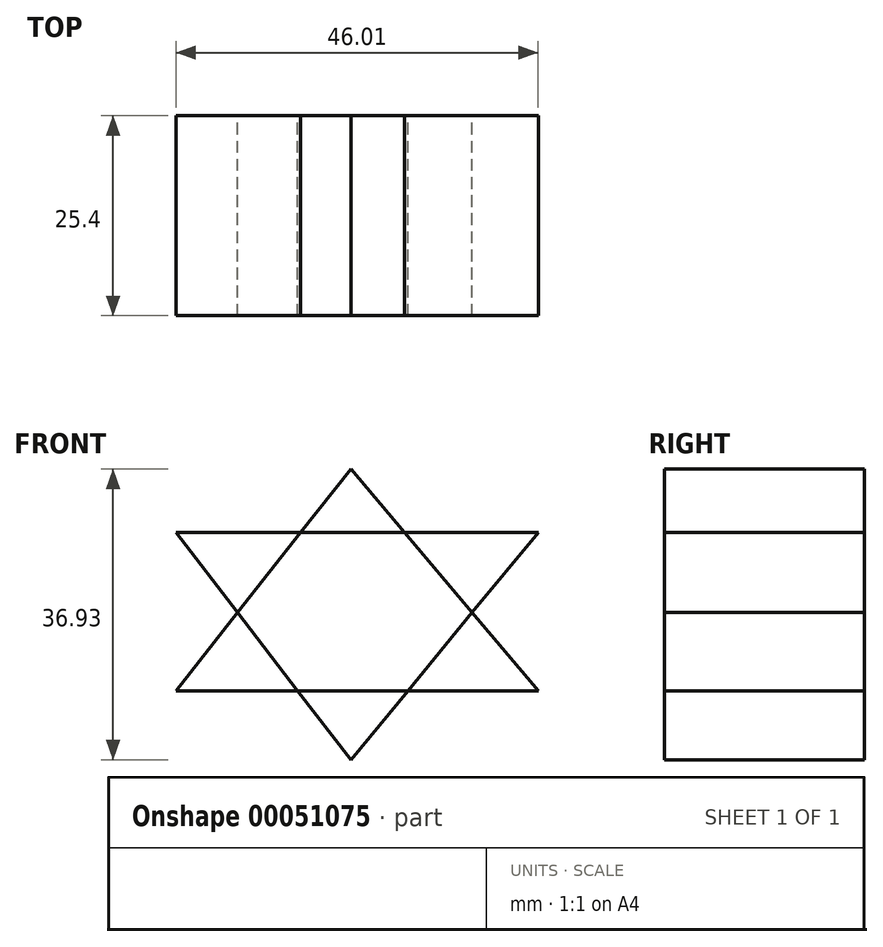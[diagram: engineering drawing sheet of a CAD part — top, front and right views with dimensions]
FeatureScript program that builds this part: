
annotation { "Feature Type Name" : "Feature", "Feature Type Description" : "" }
export const myFeature = defineFeature(function(context is Context, id is Id, definition is map)
    precondition{}
    {
        {
            var Q0;
            Q0=qCreatedBy(makeId("Front.planeOp"),FACE);
            var sketch = newSketch(context, id + "F0", { "sketchPlane" : qUnion([Q0])});
            skLineSegment(sketch, "E0", {"start": v(23.81, 0) * mm, "end": v(-22.2, 0) * mm});
            skLineSegment(sketch, "E1", {"start": v(-22.2, 0) * mm, "end": v(0, 28.15) * mm});
            skLineSegment(sketch, "E2", {"start": v(0, 28.15) * mm, "end": v(23.81, 0) * mm});
            skLineSegment(sketch, "E3", {"start": v(23.81, 20.08) * mm, "end": v(-22.2, 20.08) * mm});
            skLineSegment(sketch, "E4", {"start": v(-22.2, 20.08) * mm, "end": v(0, -8.78) * mm});
            skLineSegment(sketch, "E5", {"start": v(0, -8.78) * mm, "end": v(23.81, 20.08) * mm});
            skSolve(sketch);
        }
        {
            var Q0;
            {var subQ0=sQuery(id+"F0.wireOp",EDGE,"E3");var subQ1=sQuery(id+"F0.wireOp",EDGE,"E2");var subQ2=makeQuery(id+"F0.imprint","INTERSECT",VERTEX,{"derivedFrom":[subQ1,subQ0]});Q0=makeQuery(id+"F0.imprint","IMPRINT",FACE,{"disambiguationData":[TD([[makeQuery(id+"F0.imprint","IMPRINT",EDGE,{"disambiguationData":[TD([[subQ2,-1.0]])],"derivedFrom":subQ1}),1.0]])]});}
            var Q1;
            {var subQ0=sQuery(id+"F0.wireOp",EDGE,"E5");var subQ1=sQuery(id+"F0.wireOp",EDGE,"E0");var subQ2=makeQuery(id+"F0.imprint","INTERSECT",VERTEX,{"derivedFrom":[subQ1,subQ0]});Q1=makeQuery(id+"F0.imprint","IMPRINT",FACE,{"disambiguationData":[TD([[makeQuery(id+"F0.imprint","IMPRINT",EDGE,{"disambiguationData":[TD([[subQ2,-1.0]])],"derivedFrom":subQ1}),1.0]])]});}
            var Q2;
            {var subQ0=sQuery(id+"F0.wireOp",EDGE,"E4");var subQ1=sQuery(id+"F0.wireOp",EDGE,"E1");var subQ2=makeQuery(id+"F0.imprint","INTERSECT",VERTEX,{"derivedFrom":[subQ1,subQ0]});Q2=makeQuery(id+"F0.imprint","IMPRINT",FACE,{"disambiguationData":[TD([[makeQuery(id+"F0.imprint","IMPRINT",EDGE,{"disambiguationData":[TD([[subQ2,-1.0]])],"derivedFrom":subQ1}),1.0]])]});}
            extrude(context, id + "F1", {"entities" : qUnion([Q0, Q1, Q2]), "depth" : 25.4 * mm});
        }
        {
            var Q0;
            {var subQ0=sQuery(id+"F0.wireOp",EDGE,"E1");var subQ1=sQuery(id+"F0.wireOp",EDGE,"E0");var subQ2=makeQuery(id+"F0.imprint","INTERSECT",VERTEX,{"derivedFrom":[subQ1,subQ0]});Q0=makeQuery(id+"F0.imprint","IMPRINT",FACE,{"disambiguationData":[TD([[makeQuery(id+"F0.imprint","IMPRINT",EDGE,{"disambiguationData":[TD([[subQ2,1.0]])],"derivedFrom":subQ1}),-1.0]])]});}
            var Q1;
            {var subQ0=sQuery(id+"F0.wireOp",EDGE,"E2");var subQ1=sQuery(id+"F0.wireOp",EDGE,"E1");var subQ2=makeQuery(id+"F0.imprint","INTERSECT",VERTEX,{"derivedFrom":[subQ1,subQ0]});Q1=makeQuery(id+"F0.imprint","IMPRINT",FACE,{"disambiguationData":[TD([[makeQuery(id+"F0.imprint","IMPRINT",EDGE,{"disambiguationData":[TD([[subQ2,1.0]])],"derivedFrom":subQ1}),-1.0]])]});}
            var Q2;
            {var subQ0=sQuery(id+"F0.wireOp",EDGE,"E2");var subQ1=sQuery(id+"F0.wireOp",EDGE,"E0");var subQ2=makeQuery(id+"F0.imprint","INTERSECT",VERTEX,{"derivedFrom":[subQ1,subQ0]});Q2=makeQuery(id+"F0.imprint","IMPRINT",FACE,{"disambiguationData":[TD([[makeQuery(id+"F0.imprint","IMPRINT",EDGE,{"disambiguationData":[TD([[subQ2,-1.0]])],"derivedFrom":subQ1}),-1.0]])]});}
            extrude(context, id + "F2", {"entities" : qUnion([Q0, Q1, Q2]), "depth" : 25.4 * mm});
        }
    });
